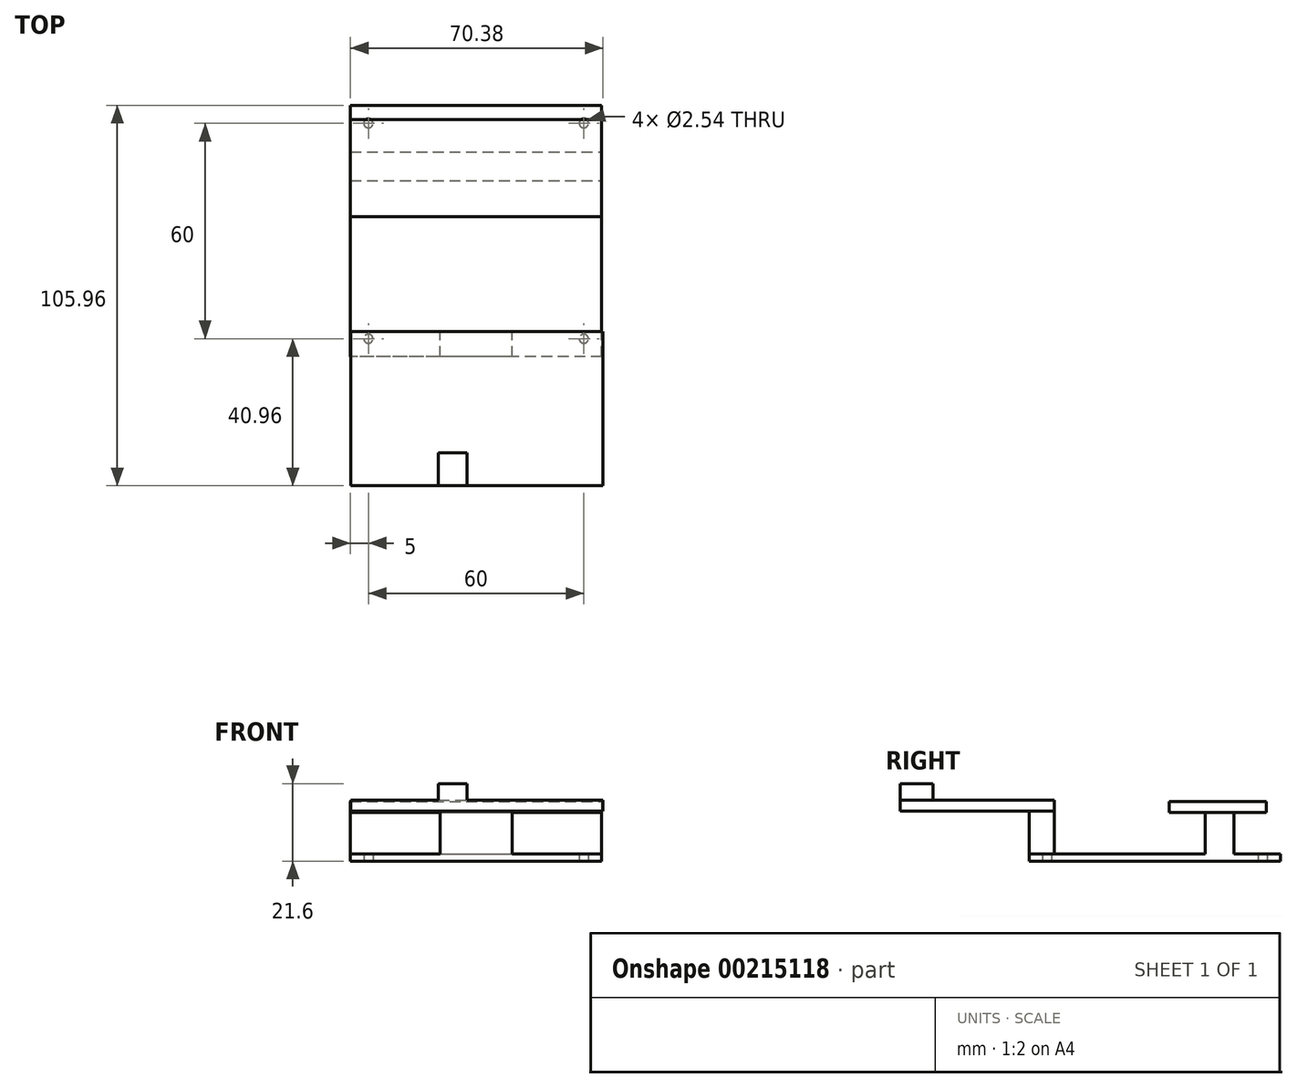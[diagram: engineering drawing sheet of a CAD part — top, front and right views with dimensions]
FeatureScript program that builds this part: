
annotation { "Feature Type Name" : "Feature", "Feature Type Description" : "" }
export const myFeature = defineFeature(function(context is Context, id is Id, definition is map)
    precondition{}
    {
        {
            var Q0;
            Q0=qCreatedBy(makeId("Top.planeOp"),FACE);
            var sketch = newSketch(context, id + "F0", { "sketchPlane" : qUnion([Q0])});
            skLineSegment(sketch, "E0.bottom", {"start": v(35, -35) * mm, "end": v(-35, -35) * mm});
            skLineSegment(sketch, "E0.top", {"start": v(35, 35) * mm, "end": v(-35, 35) * mm});
            skLineSegment(sketch, "E0.left", {"start": v(35, -35) * mm, "end": v(35, 35) * mm});
            skLineSegment(sketch, "E0.right", {"start": v(-35, -35) * mm, "end": v(-35, 35) * mm});
            skPoint(sketch, "E0.middle", {"position": v(0, 0) * mm});
            skSolve(sketch);
        }
        {
            var Q0;
            Q0 = qSketchRegion(id + "F0", true);
            extrude(context, id + "F1", {"entities" : qUnion([Q0]), "depth" : 2 * mm});
        }
        {
            var Q0;
            Q0=qCreatedBy(makeId("Top.planeOp"),FACE);
            var sketch = newSketch(context, id + "F2", { "sketchPlane" : qUnion([Q0])});
            skPoint(sketch, "E1", {"position": v(-30, 30) * mm});
            skPoint(sketch, "E2.MirrorP", {"position": v(30, 30) * mm});
            skPoint(sketch, "E3.MirrorP", {"position": v(-30, -30) * mm});
            skPoint(sketch, "E4.MirrorP", {"position": v(30, -30) * mm});
            skSolve(sketch);
        }
        {
            var Q0;
            Q0=sQuery(id+"F2.wireOp",VERTEX,"E1");
            var Q1;
            Q1=sQuery(id+"F2.wireOp",VERTEX,"E2.MirrorP");
            var Q2;
            Q2=sQuery(id+"F2.wireOp",VERTEX,"E3.MirrorP");
            var Q3;
            Q3=sQuery(id+"F2.wireOp",VERTEX,"E4.MirrorP");
            var Q4;
            Q4=makeQuery(id+"F1.opExtrude","SWEPT_BODY",BODY,{"disambiguationData":[OSD([sQuery(id+"F0.wireOp",EDGE,"E0.bottom"),sQuery(id+"F0.wireOp",EDGE,"E0.top"),sQuery(id+"F0.wireOp",EDGE,"E0.left"),sQuery(id+"F0.wireOp",EDGE,"E0.right")])]});
            hole(context, id + "F3", {"style" : HoleStyle.SIMPLE, "endStyle" : HoleEndStyle.THROUGH, "oppositeDirection" : true, "holeDiameter" : 2.54 * mm, "locations" : qUnion([Q0, Q1, Q2, Q3]), "scope" : qUnion([Q4]), "isTappedThrough" : true});
        }
        {
            var Q0;
            Q0=makeQuery(id+"F1.opExtrude","CAP_FACE",FACE,{"disambiguationData":[OSD([sQuery(id+"F0.wireOp",EDGE,"E0.bottom"),sQuery(id+"F0.wireOp",EDGE,"E0.top"),sQuery(id+"F0.wireOp",EDGE,"E0.left"),sQuery(id+"F0.wireOp",EDGE,"E0.right")])],"isStart":false});
            var sketch = newSketch(context, id + "F4", { "sketchPlane" : qUnion([Q0])});
            skLineSegment(sketch, "E5.bottom", {"start": v(-35, 22) * mm, "end": v(35, 22) * mm});
            skLineSegment(sketch, "E5.top", {"start": v(-35, 14) * mm, "end": v(35, 14) * mm});
            skLineSegment(sketch, "E5.left", {"start": v(-35, 22) * mm, "end": v(-35, 14) * mm});
            skLineSegment(sketch, "E5.right", {"start": v(35, 22) * mm, "end": v(35, 14) * mm});
            skSolve(sketch);
        }
        {
            var Q0;
            Q0 = qSketchRegion(id + "F4", true);
            extrude(context, id + "F5", {"entities" : qUnion([Q0]), "operationType" : NewBodyOperationType.ADD, "depth" : 11.6 * mm});
        }
        {
            var Q0;
            Q0=makeQuery(id+"F5.opExtrude","CAP_FACE",FACE,{"disambiguationData":[OSD([sQuery(id+"F4.wireOp",EDGE,"E5.bottom"),sQuery(id+"F4.wireOp",EDGE,"E5.top"),sQuery(id+"F4.wireOp",EDGE,"E5.left"),sQuery(id+"F4.wireOp",EDGE,"E5.right")])],"isStart":false});
            var sketch = newSketch(context, id + "F6", { "sketchPlane" : qUnion([Q0])});
            skLineSegment(sketch, "E6.bottom", {"start": v(-35, 31) * mm, "end": v(34.9, 31) * mm});
            skLineSegment(sketch, "E6.top", {"start": v(-35, 4) * mm, "end": v(34.9, 4) * mm});
            skLineSegment(sketch, "E6.left", {"start": v(-35, 31) * mm, "end": v(-35, 4) * mm});
            skLineSegment(sketch, "E6.right", {"start": v(34.9, 31) * mm, "end": v(34.9, 4) * mm});
            skSolve(sketch);
        }
        {
            var Q0;
            Q0 = qSketchRegion(id + "F6", true);
            extrude(context, id + "F7", {"entities" : qUnion([Q0]), "operationType" : NewBodyOperationType.ADD, "depth" : 3 * mm});
        }
        {
            var Q0;
            {var subQ0=sQuery(id+"F0.wireOp",EDGE,"E0.left");var subQ1=sQuery(id+"F0.wireOp",EDGE,"E0.right");var subQ2=sQuery(id+"F0.wireOp",EDGE,"E0.bottom");Q0=makeQuery(id+"F5.boolean.opBoolean","SPLIT",FACE,{"disambiguationData":[TD([makeQuery(id+"F1.opExtrude","SWEPT_FACE",FACE,{"disambiguationData":[OSD([subQ2])]})])],"derivedFrom":makeQuery(id+"F1.opExtrude","CAP_FACE",FACE,{"disambiguationData":[OSD([subQ2,sQuery(id+"F0.wireOp",EDGE,"E0.top"),subQ0,subQ1])],"isStart":false})});}
            var sketch = newSketch(context, id + "F8", { "sketchPlane" : qUnion([Q0])});
            skLineSegment(sketch, "E7.bottom", {"start": v(-10, -35) * mm, "end": v(10, -35) * mm});
            skLineSegment(sketch, "E7.top", {"start": v(-10, -28) * mm, "end": v(10, -28) * mm});
            skLineSegment(sketch, "E7.left", {"start": v(-10, -35) * mm, "end": v(-10, -28) * mm});
            skLineSegment(sketch, "E7.right", {"start": v(10, -35) * mm, "end": v(10, -28) * mm});
            skSolve(sketch);
        }
        {
            var Q0;
            Q0 = qSketchRegion(id + "F8", true);
            extrude(context, id + "F9", {"entities" : qUnion([Q0]), "operationType" : NewBodyOperationType.ADD, "depth" : 12 * mm});
        }
        {
            var Q0;
            Q0=makeQuery(id+"F9.opExtrude","CAP_FACE",FACE,{"disambiguationData":[OSD([sQuery(id+"F8.wireOp",EDGE,"E7.bottom"),sQuery(id+"F8.wireOp",EDGE,"E7.top"),sQuery(id+"F8.wireOp",EDGE,"E7.left"),sQuery(id+"F8.wireOp",EDGE,"E7.right")])],"isStart":false});
            var sketch = newSketch(context, id + "F10", { "sketchPlane" : qUnion([Q0])});
            skLineSegment(sketch, "E8.bottom", {"start": v(-34.97, -27.96) * mm, "end": v(35.38, -27.96) * mm});
            skLineSegment(sketch, "E8.top", {"start": v(-34.97, -70.96) * mm, "end": v(35.38, -70.96) * mm});
            skLineSegment(sketch, "E8.left", {"start": v(-34.97, -27.96) * mm, "end": v(-34.97, -70.96) * mm});
            skLineSegment(sketch, "E8.right", {"start": v(35.38, -27.96) * mm, "end": v(35.38, -70.96) * mm});
            skSolve(sketch);
        }
        {
            var Q0;
            Q0 = qSketchRegion(id + "F10", true);
            extrude(context, id + "F11", {"entities" : qUnion([Q0]), "operationType" : NewBodyOperationType.ADD, "depth" : 3 * mm});
        }
        {
            var Q0;
            Q0=makeQuery(id+"F11.opExtrude","CAP_FACE",FACE,{"disambiguationData":[OSD([sQuery(id+"F10.wireOp",EDGE,"E8.bottom"),sQuery(id+"F10.wireOp",EDGE,"E8.top"),sQuery(id+"F10.wireOp",EDGE,"E8.left"),sQuery(id+"F10.wireOp",EDGE,"E8.right")])],"isStart":false});
            var sketch = newSketch(context, id + "F12", { "sketchPlane" : qUnion([Q0])});
            skLineSegment(sketch, "E9.bottom", {"start": v(-10.47, -70.96) * mm, "end": v(-2.47, -70.96) * mm});
            skLineSegment(sketch, "E9.top", {"start": v(-10.47, -61.76) * mm, "end": v(-2.47, -61.76) * mm});
            skLineSegment(sketch, "E9.left", {"start": v(-10.47, -70.96) * mm, "end": v(-10.47, -61.76) * mm});
            skLineSegment(sketch, "E9.right", {"start": v(-2.47, -70.96) * mm, "end": v(-2.47, -61.76) * mm});
            skSolve(sketch);
        }
        {
            var Q0;
            Q0 = qSketchRegion(id + "F12", true);
            extrude(context, id + "F13", {"entities" : qUnion([Q0]), "operationType" : NewBodyOperationType.ADD, "depth" : 4.6 * mm});
        }
    });
